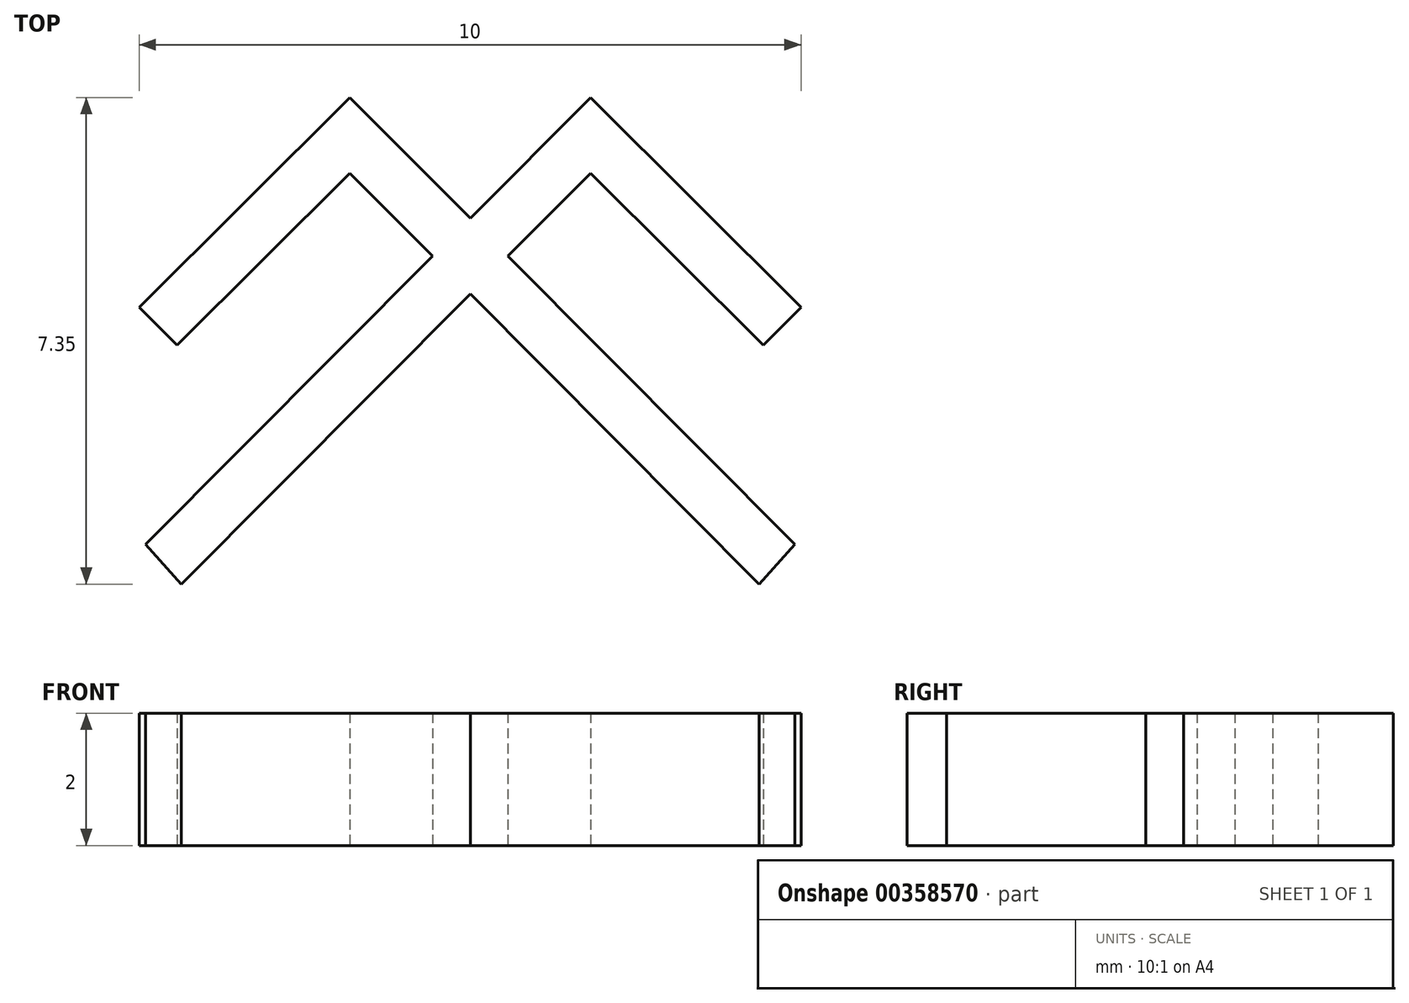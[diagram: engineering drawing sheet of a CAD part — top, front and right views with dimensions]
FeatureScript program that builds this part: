
annotation { "Feature Type Name" : "Feature", "Feature Type Description" : "" }
export const myFeature = defineFeature(function(context is Context, id is Id, definition is map)
    precondition{}
    {
        {
            var Q0;
            Q0=qCreatedBy(makeId("Top.planeOp"),FACE);
            var sketch = newSketch(context, id + "F0", { "sketchPlane" : qUnion([Q0])});
            skLineSegment(sketch, "E0", {"start": v(-4.9, -3.7) * mm, "end": v(1.82, 3.04) * mm});
            skLineSegment(sketch, "E1", {"start": v(1.82, 3.04) * mm, "end": v(5, -0.13) * mm});
            skLineSegment(sketch, "E2", {"start": v(5, -0.13) * mm, "end": v(4.43, -0.7) * mm});
            skLineSegment(sketch, "E3", {"start": v(4.43, -0.7) * mm, "end": v(1.82, 1.9) * mm});
            skLineSegment(sketch, "E4", {"start": v(1.82, 1.9) * mm, "end": v(-4.36, -4.3) * mm});
            skLineSegment(sketch, "E5", {"start": v(-4.36, -4.3) * mm, "end": v(-4.9, -3.7) * mm});
            skLineSegment(sketch, "E6", {"start": v(0, 1.22) * mm, "end": v(0, 0.07) * mm});
            skLineSegment(sketch, "E7.MirrorCS", {"start": v(-1.82, 1.9) * mm, "end": v(4.37, -4.3) * mm});
            skLineSegment(sketch, "E8.MirrorCS", {"start": v(4.9, -3.7) * mm, "end": v(-1.82, 3.04) * mm});
            skLineSegment(sketch, "E9.MirrorCS", {"start": v(-1.82, 3.04) * mm, "end": v(-5, -0.13) * mm});
            skLineSegment(sketch, "E10.MirrorCS", {"start": v(-5, -0.13) * mm, "end": v(-4.43, -0.7) * mm});
            skLineSegment(sketch, "E11.MirrorCS", {"start": v(-4.43, -0.7) * mm, "end": v(-1.82, 1.9) * mm});
            skLineSegment(sketch, "E12.MirrorCS", {"start": v(4.37, -4.3) * mm, "end": v(4.9, -3.7) * mm});
            skSolve(sketch);
        }
        {
            var Q0;
            Q0 = qSketchRegion(id + "F0", true);
            extrude(context, id + "F1", {"entities" : qUnion([Q0]), "depth" : 2 * mm});
        }
    });
